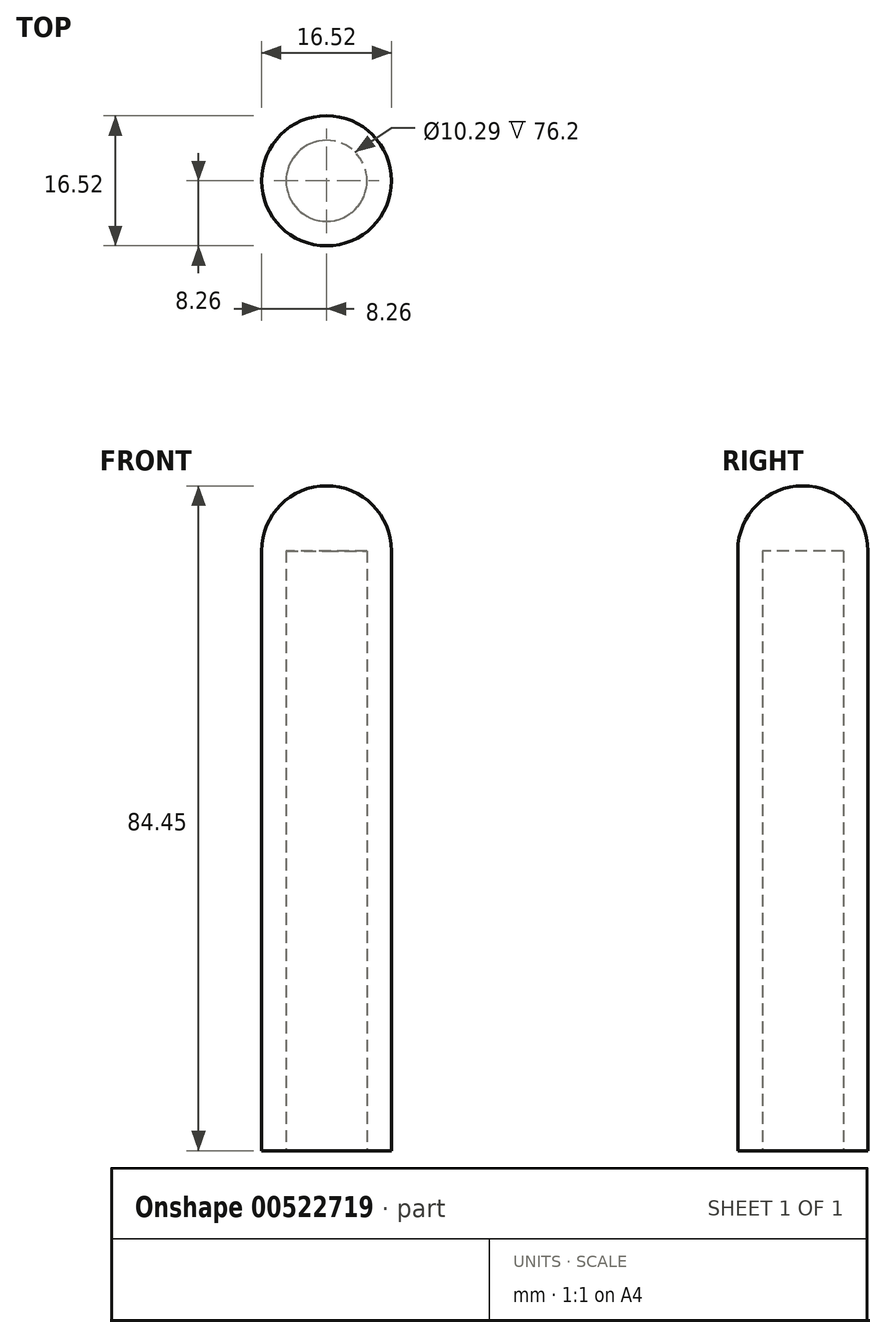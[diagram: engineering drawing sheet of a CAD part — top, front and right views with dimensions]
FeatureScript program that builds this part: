
annotation { "Feature Type Name" : "Feature", "Feature Type Description" : "" }
export const myFeature = defineFeature(function(context is Context, id is Id, definition is map)
    precondition{}
    {
        {
            var Q0;
            Q0=qCreatedBy(makeId("Top.planeOp"),FACE);
            var sketch = newSketch(context, id + "F0", { "sketchPlane" : qUnion([Q0])});
            skCircle(sketch, "E0", {"center": v(0, 0) * mm, "radius": 5.14 * mm});
            skCircle(sketch, "E1", {"center": v(0, 0) * mm, "radius": 8.26 * mm});
            skSolve(sketch);
        }
        {
            var Q0;
            Q0 = qSketchRegion(id + "F0", true);
            extrude(context, id + "F1", {"entities" : qUnion([Q0]), "depth" : 76.2 * mm, "offsetDistance" : 25.4 * mm});
        }
        {
            var Q0;
            Q0=makeQuery(id+"F1.opExtrude","CAP_FACE",FACE,{"disambiguationData":[OSD([sQuery(id+"F0.wireOp",EDGE,"E0"),sQuery(id+"F0.wireOp",EDGE,"E1")])],"isStart":false});
            var sketch = newSketch(context, id + "F2", { "sketchPlane" : qUnion([Q0])});
            skArc(sketch, "E2", {"start": v(8.26, 0) * mm, "mid": v(0, 8.26) * mm, "end": v(-8.26, 0) * mm});
            skLineSegment(sketch, "E3", {"start": v(-8.26, 0) * mm, "end": v(8.26, 0) * mm});
            skSolve(sketch);
        }
        {
            var Q0;
            Q0 = qSketchRegion(id + "F2", true);
            var Q1;
            Q1=sQuery(id+"F2.wireOp",EDGE,"E3");
            revolve(context, id + "F3", {"operationType" : NewBodyOperationType.ADD, "entities" : qUnion([Q0]), "axis" : qUnion([Q1]), "revolveType" : RevolveType.ONE_DIRECTION, "angle" : 180 * degree});
        }
    });
